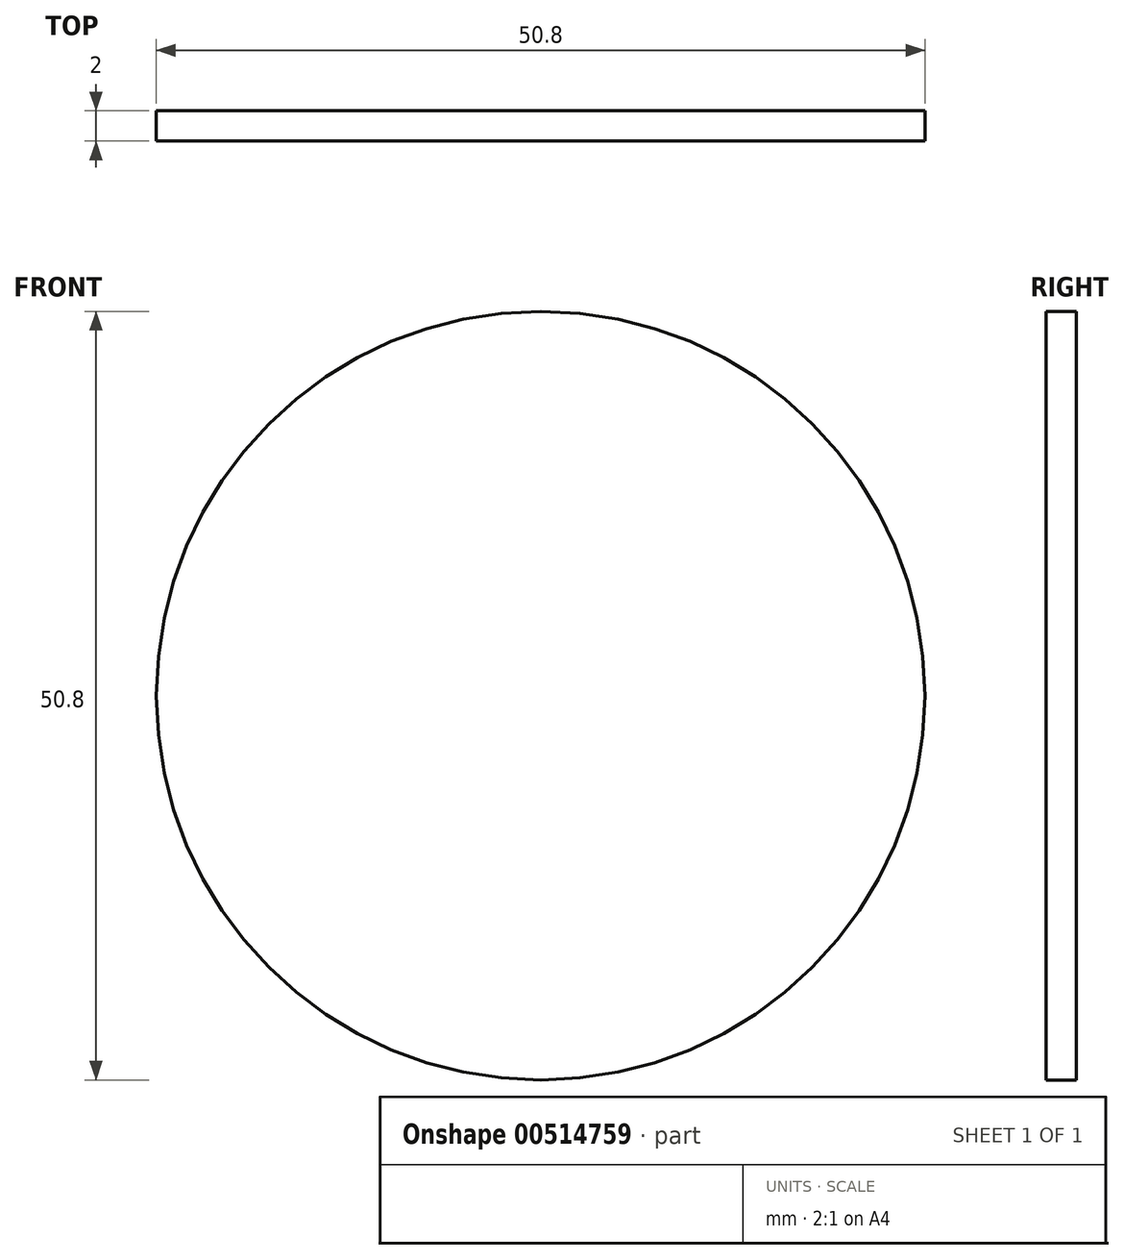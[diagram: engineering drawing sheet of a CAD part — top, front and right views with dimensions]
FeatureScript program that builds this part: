
annotation { "Feature Type Name" : "Feature", "Feature Type Description" : "" }
export const myFeature = defineFeature(function(context is Context, id is Id, definition is map)
    precondition{}
    {
        {
            var Q0;
            Q0=qCreatedBy(makeId("Front.planeOp"),FACE);
            var sketch = newSketch(context, id + "F0", { "sketchPlane" : qUnion([Q0])});
            skCircle(sketch, "E0", {"center": v(0, 0) * mm, "radius": 25.4 * mm});
            skSolve(sketch);
        }
        {
            var Q0;
            Q0 = qSketchRegion(id + "F0", true);
            extrude(context, id + "F1", {"entities" : qUnion([Q0]), "oppositeDirection" : true, "depth" : 2 * mm, "offsetDistance" : 25 * mm});
        }
    });
